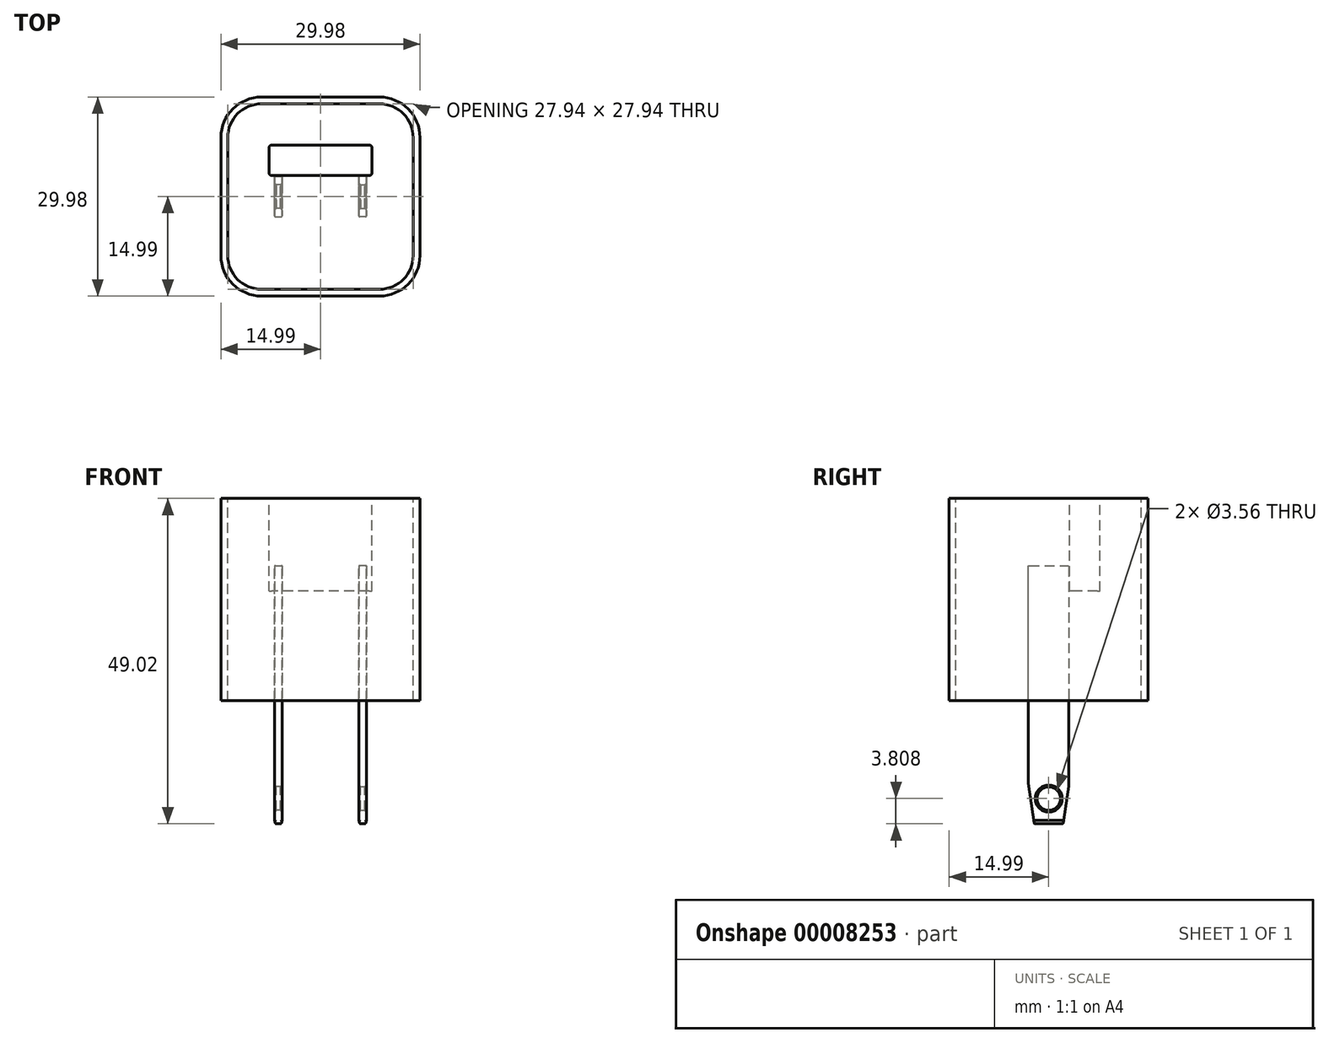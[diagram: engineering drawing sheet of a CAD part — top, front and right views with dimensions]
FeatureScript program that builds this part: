
annotation { "Feature Type Name" : "Feature", "Feature Type Description" : "" }
export const myFeature = defineFeature(function(context is Context, id is Id, definition is map)
    precondition{}
    {
        {
            var Q0;
            Q0=qCreatedBy(makeId("Top.planeOp"),FACE);
            var sketch = newSketch(context, id + "F0", { "sketchPlane" : qUnion([Q0])});
            skLineSegment(sketch, "E0.rect.bottom", {"start": v(8.9, 13.97) * mm, "end": v(-8.89, 13.97) * mm});
            skLineSegment(sketch, "E0.rect.top", {"start": v(8.9, -13.97) * mm, "end": v(-8.89, -13.97) * mm});
            skLineSegment(sketch, "E0.rect.left", {"start": v(13.97, 8.9) * mm, "end": v(13.97, -8.9) * mm});
            skLineSegment(sketch, "E0.rect.right", {"start": v(-13.97, 8.9) * mm, "end": v(-13.97, -8.89) * mm});
            skPoint(sketch, "E0.rect.middle", {"position": v(0, 0) * mm});
            skPoint(sketch, "E1.visualSharp", {"position": v(-13.97, 13.97) * mm});
            skArc(sketch, "E1.filletArc", {"start": v(-8.89, 13.97) * mm, "mid": v(-12.48, 12.48) * mm, "end": v(-13.97, 8.9) * mm});
            skPoint(sketch, "E2.visualSharp", {"position": v(13.97, 13.97) * mm});
            skArc(sketch, "E2.filletArc", {"start": v(13.97, 8.9) * mm, "mid": v(12.48, 12.48) * mm, "end": v(8.9, 13.97) * mm});
            skPoint(sketch, "E3.visualSharp", {"position": v(13.97, -13.97) * mm});
            skArc(sketch, "E3.filletArc", {"start": v(8.9, -13.97) * mm, "mid": v(12.48, -12.48) * mm, "end": v(13.97, -8.9) * mm});
            skPoint(sketch, "E4.visualSharp", {"position": v(-13.97, -13.97) * mm});
            skArc(sketch, "E4.filletArc", {"start": v(-13.97, -8.9) * mm, "mid": v(-12.48, -12.48) * mm, "end": v(-8.89, -13.97) * mm});
            skArc(sketch, "E5.0", {"start": v(14.99, 8.89) * mm, "mid": v(13.2, 13.2) * mm, "end": v(8.89, 14.99) * mm});
            skLineSegment(sketch, "E5.1", {"start": v(14.99, 8.89) * mm, "end": v(14.99, -8.89) * mm});
            skArc(sketch, "E5.2", {"start": v(8.9, -14.99) * mm, "mid": v(13.2, -13.2) * mm, "end": v(14.99, -8.89) * mm});
            skLineSegment(sketch, "E5.3", {"start": v(8.9, -14.99) * mm, "end": v(-8.89, -14.99) * mm});
            skArc(sketch, "E5.4", {"start": v(-14.99, -8.89) * mm, "mid": v(-13.2, -13.2) * mm, "end": v(-8.89, -14.99) * mm});
            skLineSegment(sketch, "E5.5", {"start": v(8.89, 14.99) * mm, "end": v(-8.89, 14.99) * mm});
            skLineSegment(sketch, "E5.6", {"start": v(-14.99, 8.9) * mm, "end": v(-14.99, -8.89) * mm});
            skArc(sketch, "E5.7", {"start": v(-8.89, 14.99) * mm, "mid": v(-13.2, 13.2) * mm, "end": v(-14.99, 8.9) * mm});
            skSolve(sketch);
        }
        {
            var Q0;
            Q0=makeQuery(id+"F0.imprint","IMPRINT",FACE,{"disambiguationData":[TD([[makeQuery(id+"F0.imprint","IMPRINT",EDGE,{"derivedFrom":sQuery(id+"F0.wireOp",EDGE,"E0.rect.bottom")}),1.0]])]});
            extrude(context, id + "F1", {"entities" : qUnion([Q0]), "oppositeDirection" : true, "depth" : 30.48 * mm});
        }
        {
            var Q0;
            Q0=makeQuery(id+"F0.imprint","IMPRINT",FACE,{"disambiguationData":[TD([[makeQuery(id+"F0.imprint","IMPRINT",EDGE,{"derivedFrom":sQuery(id+"F0.wireOp",EDGE,"E0.rect.bottom")}),-1.0]])]});
            var Q1;
            Q1=makeQuery(id+"F1.opExtrude","CAP_FACE",FACE,{"disambiguationData":[OSD([sQuery(id+"F0.wireOp",EDGE,"E0.rect.bottom"),sQuery(id+"F0.wireOp",EDGE,"E0.rect.top"),sQuery(id+"F0.wireOp",EDGE,"E0.rect.left"),sQuery(id+"F0.wireOp",EDGE,"E0.rect.right"),sQuery(id+"F0.wireOp",EDGE,"E1.filletArc"),sQuery(id+"F0.wireOp",EDGE,"E2.filletArc"),sQuery(id+"F0.wireOp",EDGE,"E3.filletArc"),sQuery(id+"F0.wireOp",EDGE,"E4.filletArc")])],"isStart":false});
            extrude(context, id + "F2", {"entities" : qUnion([Q0]), "endBound" : BoundingType.UP_TO_SURFACE, "oppositeDirection" : true, "endBoundEntityFace" : qUnion([Q1]), "depth" : 25.4 * mm});
        }
        {
            var Q0;
            Q0=makeQuery(id+"F1.opExtrude","CAP_FACE",FACE,{"disambiguationData":[OSD([sQuery(id+"F0.wireOp",EDGE,"E0.rect.bottom"),sQuery(id+"F0.wireOp",EDGE,"E0.rect.top"),sQuery(id+"F0.wireOp",EDGE,"E0.rect.left"),sQuery(id+"F0.wireOp",EDGE,"E0.rect.right"),sQuery(id+"F0.wireOp",EDGE,"E1.filletArc"),sQuery(id+"F0.wireOp",EDGE,"E2.filletArc"),sQuery(id+"F0.wireOp",EDGE,"E3.filletArc"),sQuery(id+"F0.wireOp",EDGE,"E4.filletArc")])],"isStart":true});
            var sketch = newSketch(context, id + "F3", { "sketchPlane" : qUnion([Q0])});
            skLineSegment(sketch, "E6", {"start": v(0, 0) * mm, "end": v(0, 5.46) * mm, "construction": true});
            skLineSegment(sketch, "E7.rect.bottom", {"start": v(7.37, 7.75) * mm, "end": v(-7.37, 7.75) * mm});
            skLineSegment(sketch, "E7.rect.top", {"start": v(7.37, 3.18) * mm, "end": v(-7.37, 3.17) * mm});
            skLineSegment(sketch, "E7.rect.left", {"start": v(7.75, 7.37) * mm, "end": v(7.75, 3.56) * mm});
            skLineSegment(sketch, "E7.rect.right", {"start": v(-7.75, 7.37) * mm, "end": v(-7.75, 3.56) * mm});
            skPoint(sketch, "E7.rect.middle", {"position": v(0, 5.46) * mm});
            skPoint(sketch, "E8.visualSharp", {"position": v(-7.75, 7.75) * mm});
            skArc(sketch, "E8.filletArc", {"start": v(-7.37, 7.75) * mm, "mid": v(-7.64, 7.64) * mm, "end": v(-7.75, 7.37) * mm});
            skPoint(sketch, "E9.visualSharp", {"position": v(-7.75, 3.17) * mm});
            skArc(sketch, "E9.filletArc", {"start": v(-7.75, 3.56) * mm, "mid": v(-7.64, 3.29) * mm, "end": v(-7.37, 3.17) * mm});
            skPoint(sketch, "E10.visualSharp", {"position": v(7.75, 3.18) * mm});
            skArc(sketch, "E10.filletArc", {"start": v(7.37, 3.18) * mm, "mid": v(7.64, 3.29) * mm, "end": v(7.75, 3.56) * mm});
            skPoint(sketch, "E11.visualSharp", {"position": v(7.75, 7.75) * mm});
            skArc(sketch, "E11.filletArc", {"start": v(7.75, 7.37) * mm, "mid": v(7.64, 7.64) * mm, "end": v(7.37, 7.75) * mm});
            skSolve(sketch);
        }
        {
            var Q0;
            Q0 = qSketchRegion(id + "F3", true);
            extrude(context, id + "F4", {"entities" : qUnion([Q0]), "operationType" : NewBodyOperationType.REMOVE, "oppositeDirection" : true, "depth" : 13.97 * mm});
        }
        {
            var Q0;
            Q0=qCreatedBy(makeId("Right.planeOp"),FACE);
            cPlane(context, id + "F5", {"entities" : qUnion([Q0]), "cplaneType" : CPlaneType.OFFSET, "offset" : 6.35 * mm, "width" : 152.4 * mm, "height" : 152.4 * mm});
        }
        {
            var Q0;
            Q0=qCreatedBy(id+"F5.planeOp",FACE);
            var sketch = newSketch(context, id + "F6", { "sketchPlane" : qUnion([Q0])});
            skLineSegment(sketch, "E12", {"start": v(3.05, -10.16) * mm, "end": v(3.05, -43.18) * mm});
            skLineSegment(sketch, "E13", {"start": v(3.05, -43.18) * mm, "end": v(2.16, -49.02) * mm});
            skLineSegment(sketch, "E14", {"start": v(2.16, -49.02) * mm, "end": v(-2.16, -49.02) * mm});
            skLineSegment(sketch, "E15", {"start": v(-2.16, -49.02) * mm, "end": v(-3.05, -43.18) * mm});
            skLineSegment(sketch, "E16", {"start": v(-3.05, -43.18) * mm, "end": v(-3.05, -10.16) * mm});
            skLineSegment(sketch, "E17", {"start": v(-3.05, -10.16) * mm, "end": v(3.05, -10.16) * mm});
            skLineSegment(sketch, "E18", {"start": v(0, 0) * mm, "end": v(0, -10.16) * mm, "construction": true});
            skSolve(sketch);
        }
        {
            var Q0;
            Q0=makeQuery(id+"F6.imprint","IMPRINT",FACE,{"disambiguationData":[TD([[makeQuery(id+"F6.imprint","IMPRINT",EDGE,{"derivedFrom":sQuery(id+"F6.wireOp",EDGE,"E12")}),-1.0]])]});
            extrude(context, id + "F7", {"entities" : qUnion([Q0]), "endBound" : BoundingType.SYMMETRIC, "depth" : 1.14 * mm});
        }
        {
            var Q0;
            Q0=makeQuery(id+"F7.opExtrude","CAP_FACE",FACE,{"disambiguationData":[OSD([sQuery(id+"F6.wireOp",EDGE,"E12"),sQuery(id+"F6.wireOp",EDGE,"E13"),sQuery(id+"F6.wireOp",EDGE,"E14"),sQuery(id+"F6.wireOp",EDGE,"E15"),sQuery(id+"F6.wireOp",EDGE,"E16"),sQuery(id+"F6.wireOp",EDGE,"E17")])],"isStart":false});
            var sketch = newSketch(context, id + "F8", { "sketchPlane" : qUnion([Q0])});
            skLineSegment(sketch, "E19.0", {"start": v(2.16, -49.02) * mm, "end": v(-2.16, -49.02) * mm});
            skLineSegment(sketch, "E20", {"start": v(0, -49.02) * mm, "end": v(0, -45.21) * mm, "construction": true});
            skCircle(sketch, "E21", {"center": v(0, -45.21) * mm, "radius": 1.78 * mm});
            skSolve(sketch);
        }
        {
            var Q0;
            Q0 = qSketchRegion(id + "F8", true);
            extrude(context, id + "F9", {"entities" : qUnion([Q0]), "operationType" : NewBodyOperationType.REMOVE, "endBound" : BoundingType.UP_TO_NEXT, "oppositeDirection" : true, "depth" : 25.4 * mm});
        }
        {
            var Q0;
            Q0=makeQuery(id+"F9.boolean.opBoolean","COPY",FACE,{"derivedFrom":makeQuery(id+"F9.opExtrude","SWEPT_FACE",FACE,{"disambiguationData":[OSD([sQuery(id+"F8.wireOp",EDGE,"E21")])]})});
            chamfer(context, id + "F10", {"entities" : qUnion([Q0]), "width" : 0.25 * mm, "tangentPropagation" : true});
        }
        {
            var Q0;
            Q0=makeQuery(id+"F7.opExtrude","CAP_EDGE",EDGE,{"disambiguationData":[OSD([sQuery(id+"F6.wireOp",EDGE,"E14")])],"isStart":false});
            var Q1;
            Q1=makeQuery(id+"F7.opExtrude","CAP_EDGE",EDGE,{"disambiguationData":[OSD([sQuery(id+"F6.wireOp",EDGE,"E14")])],"isStart":true});
            chamfer(context, id + "F11", {"entities" : qUnion([Q0, Q1]), "chamferType" : ChamferType.TWO_OFFSETS, "width1" : 0.13 * mm, "oppositeDirection" : false, "width2" : 0.5 * mm, "tangentPropagation" : true});
        }
        {
            var Q0;
            Q0=makeQuery(id+"F7.opExtrude","SWEPT_EDGE",EDGE,{"disambiguationData":[OSD([sQuery(id+"F6.wireOp",EDGE,"E12"),sQuery(id+"F6.wireOp",EDGE,"E13")])]});
            var Q1;
            Q1=makeQuery(id+"F7.opExtrude","SWEPT_EDGE",EDGE,{"disambiguationData":[OSD([sQuery(id+"F6.wireOp",EDGE,"E15"),sQuery(id+"F6.wireOp",EDGE,"E16")])]});
            fillet(context, id + "F12", {"entities" : qUnion([Q0, Q1]), "radius" : 2.03 * mm, "tangentPropagation" : true, "allowEdgeOverflow" : false});
        }
        {
            var Q0;
            Q0=makeQuery(id+"F7.opExtrude","SWEPT_FACE",FACE,{"disambiguationData":[OSD([sQuery(id+"F6.wireOp",EDGE,"E12")])]});
            var Q1;
            Q1=makeQuery(id+"F7.opExtrude","CAP_EDGE",EDGE,{"disambiguationData":[OSD([sQuery(id+"F6.wireOp",EDGE,"E13")])],"isStart":false});
            var Q2;
            Q2=makeQuery(id+"F7.opExtrude","CAP_EDGE",EDGE,{"disambiguationData":[OSD([sQuery(id+"F6.wireOp",EDGE,"E13")])],"isStart":true});
            var Q3;
            Q3=makeQuery(id+"F11.opChamfer","BLEND_EDGE",EDGE,{"blendedFrom":[makeQuery(id+"F7.opExtrude","CAP_EDGE",EDGE,{"disambiguationData":[OSD([sQuery(id+"F6.wireOp",EDGE,"E14")])],"isStart":false}),makeQuery(id+"F7.opExtrude","SWEPT_FACE",FACE,{"disambiguationData":[OSD([sQuery(id+"F6.wireOp",EDGE,"E13")])]})],"blendedInto":[makeQuery(id+"F7.opExtrude","SWEPT_FACE",FACE,{"disambiguationData":[OSD([sQuery(id+"F6.wireOp",EDGE,"E13")])]})]});
            var Q4;
            Q4=makeQuery(id+"F11.opChamfer","BLEND_EDGE",EDGE,{"blendedFrom":[makeQuery(id+"F7.opExtrude","CAP_EDGE",EDGE,{"disambiguationData":[OSD([sQuery(id+"F6.wireOp",EDGE,"E14")])],"isStart":true}),makeQuery(id+"F7.opExtrude","SWEPT_FACE",FACE,{"disambiguationData":[OSD([sQuery(id+"F6.wireOp",EDGE,"E13")])]})],"blendedInto":[makeQuery(id+"F7.opExtrude","SWEPT_FACE",FACE,{"disambiguationData":[OSD([sQuery(id+"F6.wireOp",EDGE,"E13")])]})]});
            var Q5;
            Q5=makeQuery(id+"F7.opExtrude","SWEPT_EDGE",EDGE,{"disambiguationData":[OSD([sQuery(id+"F6.wireOp",EDGE,"E13"),sQuery(id+"F6.wireOp",EDGE,"E14")])]});
            var Q6;
            {var subQ0=sQuery(id+"F6.wireOp",EDGE,"E14");Q6=makeQuery(id+"F11.opChamfer","BLEND_EDGE",EDGE,{"blendedFrom":[makeQuery(id+"F7.opExtrude","CAP_EDGE",EDGE,{"disambiguationData":[OSD([subQ0])],"isStart":true}),makeQuery(id+"F7.opExtrude","SWEPT_FACE",FACE,{"disambiguationData":[OSD([subQ0])]})],"blendedInto":[makeQuery(id+"F7.opExtrude","SWEPT_FACE",FACE,{"disambiguationData":[OSD([subQ0])]})]});}
            var Q7;
            {var subQ0=sQuery(id+"F6.wireOp",EDGE,"E14");Q7=makeQuery(id+"F11.opChamfer","BLEND_EDGE",EDGE,{"blendedFrom":[makeQuery(id+"F7.opExtrude","CAP_EDGE",EDGE,{"disambiguationData":[OSD([subQ0])],"isStart":false}),makeQuery(id+"F7.opExtrude","SWEPT_FACE",FACE,{"disambiguationData":[OSD([subQ0])]})],"blendedInto":[makeQuery(id+"F7.opExtrude","SWEPT_FACE",FACE,{"disambiguationData":[OSD([subQ0])]})]});}
            var Q8;
            Q8=makeQuery(id+"F7.opExtrude","SWEPT_EDGE",EDGE,{"disambiguationData":[OSD([sQuery(id+"F6.wireOp",EDGE,"E14"),sQuery(id+"F6.wireOp",EDGE,"E15")])]});
            var Q9;
            Q9=makeQuery(id+"F11.opChamfer","BLEND_EDGE",EDGE,{"blendedFrom":[makeQuery(id+"F7.opExtrude","CAP_EDGE",EDGE,{"disambiguationData":[OSD([sQuery(id+"F6.wireOp",EDGE,"E14")])],"isStart":true}),makeQuery(id+"F7.opExtrude","SWEPT_FACE",FACE,{"disambiguationData":[OSD([sQuery(id+"F6.wireOp",EDGE,"E15")])]})],"blendedInto":[makeQuery(id+"F7.opExtrude","SWEPT_FACE",FACE,{"disambiguationData":[OSD([sQuery(id+"F6.wireOp",EDGE,"E15")])]})]});
            var Q10;
            Q10=makeQuery(id+"F7.opExtrude","CAP_EDGE",EDGE,{"disambiguationData":[OSD([sQuery(id+"F6.wireOp",EDGE,"E15")])],"isStart":true});
            var Q11;
            Q11=makeQuery(id+"F7.opExtrude","CAP_EDGE",EDGE,{"disambiguationData":[OSD([sQuery(id+"F6.wireOp",EDGE,"E16")])],"isStart":true});
            var Q12;
            Q12=makeQuery(id+"F11.opChamfer","BLEND_EDGE",EDGE,{"blendedFrom":[makeQuery(id+"F7.opExtrude","CAP_EDGE",EDGE,{"disambiguationData":[OSD([sQuery(id+"F6.wireOp",EDGE,"E14")])],"isStart":false}),makeQuery(id+"F7.opExtrude","SWEPT_FACE",FACE,{"disambiguationData":[OSD([sQuery(id+"F6.wireOp",EDGE,"E15")])]})],"blendedInto":[makeQuery(id+"F7.opExtrude","SWEPT_FACE",FACE,{"disambiguationData":[OSD([sQuery(id+"F6.wireOp",EDGE,"E15")])]})]});
            var Q13;
            Q13=makeQuery(id+"F7.opExtrude","CAP_EDGE",EDGE,{"disambiguationData":[OSD([sQuery(id+"F6.wireOp",EDGE,"E15")])],"isStart":false});
            var Q14;
            Q14=makeQuery(id+"F7.opExtrude","CAP_EDGE",EDGE,{"disambiguationData":[OSD([sQuery(id+"F6.wireOp",EDGE,"E16")])],"isStart":false});
            var Q15;
            Q15=makeQuery(id+"F7.opExtrude","CAP_EDGE",EDGE,{"disambiguationData":[OSD([sQuery(id+"F6.wireOp",EDGE,"E12")])],"isStart":false});
            var Q16;
            Q16=makeQuery(id+"F7.opExtrude","CAP_EDGE",EDGE,{"disambiguationData":[OSD([sQuery(id+"F6.wireOp",EDGE,"E12")])],"isStart":true});
            fillet(context, id + "F13", {"entities" : qUnion([Q0, Q1, Q2, Q3, Q4, Q5, Q6, Q7, Q8, Q9, Q10, Q11, Q12, Q13, Q14, Q15, Q16]), "radius" : 0.13 * mm, "tangentPropagation" : true, "allowEdgeOverflow" : false});
        }
        {
            var Q0;
            Q0=makeQuery(id+"F7.opExtrude","SWEPT_BODY",BODY,{"disambiguationData":[OSD([sQuery(id+"F6.wireOp",EDGE,"E12"),sQuery(id+"F6.wireOp",EDGE,"E13"),sQuery(id+"F6.wireOp",EDGE,"E14"),sQuery(id+"F6.wireOp",EDGE,"E15"),sQuery(id+"F6.wireOp",EDGE,"E16"),sQuery(id+"F6.wireOp",EDGE,"E17")])]});
            var Q1;
            Q1=qCreatedBy(makeId("Right.planeOp"),FACE);
            mirror(context, id + "F14", {"entities" : qUnion([Q0]), "mirrorPlane" : qUnion([Q1])});
        }
    });
